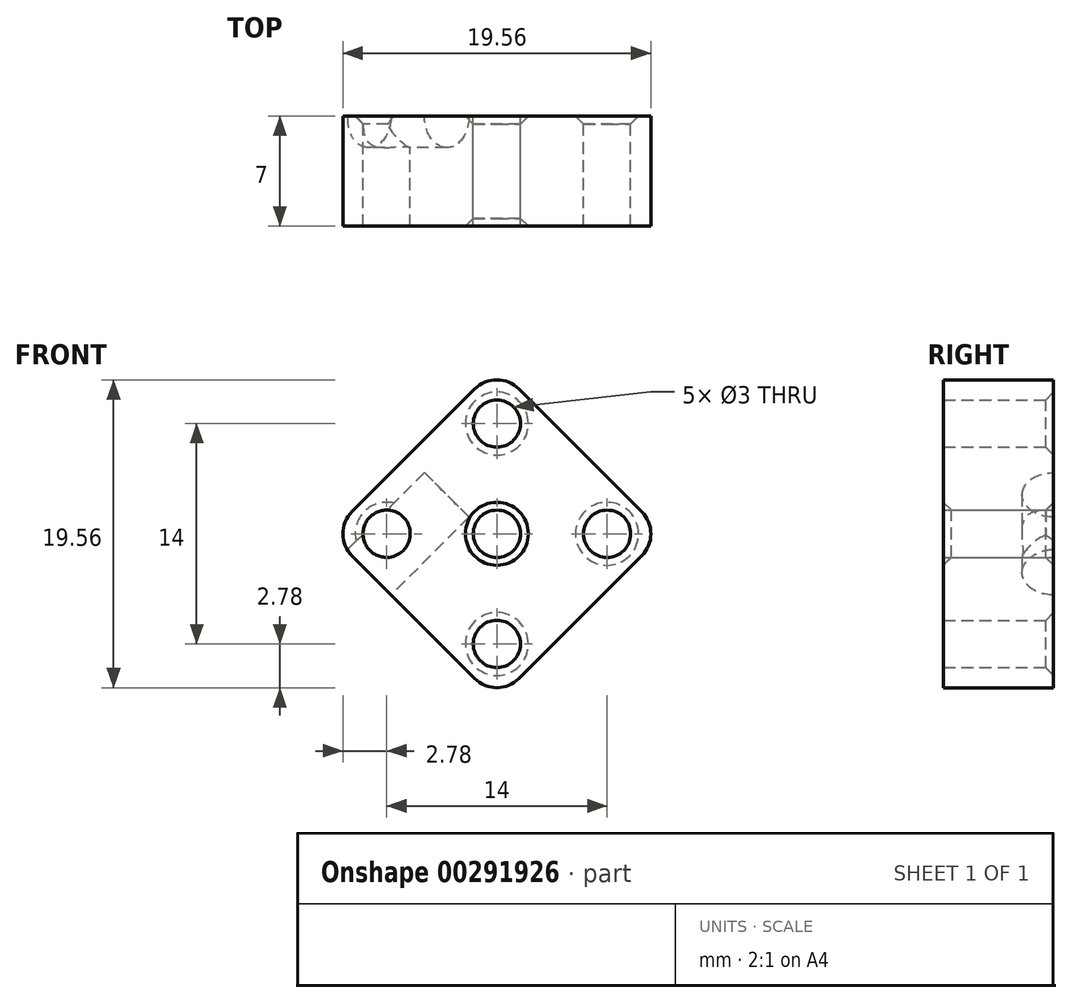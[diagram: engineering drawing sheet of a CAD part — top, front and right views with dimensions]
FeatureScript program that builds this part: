
annotation { "Feature Type Name" : "Feature", "Feature Type Description" : "" }
export const myFeature = defineFeature(function(context is Context, id is Id, definition is map)
    precondition{}
    {
        {
            var Q0;
            Q0=qCreatedBy(makeId("Front.planeOp"),FACE);
            var sketch = newSketch(context, id + "F0", { "sketchPlane" : qUnion([Q0])});
            skLineSegment(sketch, "E0.bottom", {"start": v(-1.41, -9.2) * mm, "end": v(-9.2, -1.41) * mm});
            skLineSegment(sketch, "E0.top", {"start": v(9.2, 1.41) * mm, "end": v(1.41, 9.2) * mm});
            skLineSegment(sketch, "E0.left", {"start": v(1.41, -9.2) * mm, "end": v(9.2, -1.41) * mm});
            skLineSegment(sketch, "E0.right", {"start": v(-9.2, 1.41) * mm, "end": v(-1.41, 9.2) * mm});
            skCircle(sketch, "E1", {"center": v(0, 7) * mm, "radius": 1.5 * mm});
            skCircle(sketch, "E2", {"center": v(0, 0) * mm, "radius": 1.5 * mm});
            skCircle(sketch, "E3.1.1", {"center": v(-7, 0) * mm, "radius": 1.5 * mm});
            skCircle(sketch, "E3.2.1", {"center": v(0, -7) * mm, "radius": 1.5 * mm});
            skCircle(sketch, "E3.3.1", {"center": v(7, 0) * mm, "radius": 1.5 * mm});
            skPoint(sketch, "E4.visualSharp", {"position": v(-10.6, 0) * mm});
            skArc(sketch, "E4.filletArc", {"start": v(-9.2, 1.41) * mm, "mid": v(-9.78, 0) * mm, "end": v(-9.2, -1.41) * mm});
            skPoint(sketch, "E5.visualSharp", {"position": v(0, -10.6) * mm});
            skArc(sketch, "E5.filletArc", {"start": v(-1.41, -9.2) * mm, "mid": v(0, -9.78) * mm, "end": v(1.41, -9.2) * mm});
            skPoint(sketch, "E6.visualSharp", {"position": v(10.6, 0) * mm});
            skArc(sketch, "E6.filletArc", {"start": v(9.2, -1.41) * mm, "mid": v(9.78, 0) * mm, "end": v(9.2, 1.41) * mm});
            skPoint(sketch, "E7.visualSharp", {"position": v(0, 10.6) * mm});
            skArc(sketch, "E7.filletArc", {"start": v(1.41, 9.2) * mm, "mid": v(0, 9.78) * mm, "end": v(-1.41, 9.2) * mm});
            skSolve(sketch);
        }
        {
            var Q0;
            Q0=makeQuery(id+"F0.imprint","IMPRINT",FACE,{"disambiguationData":[TD([[makeQuery(id+"F0.imprint","IMPRINT",EDGE,{"derivedFrom":sQuery(id+"F0.wireOp",EDGE,"E0.bottom")}),-1.0]])]});
            extrude(context, id + "F1", {"entities" : qUnion([Q0]), "depth" : 7 * mm});
        }
        {
            var Q0;
            Q0=makeQuery(id+"F1.opExtrude","SWEPT_FACE",FACE,{"disambiguationData":[OSD([sQuery(id+"F0.wireOp",EDGE,"E0.bottom")])]});
            var sketch = newSketch(context, id + "F2", { "sketchPlane" : qUnion([Q0])});
            skCircle(sketch, "E8", {"center": v(0, 4) * mm, "radius": 2 * mm});
            skSolve(sketch);
        }
        {
            var Q0;
            Q0=makeQuery(id+"F2.imprint","IMPRINT",FACE,{"disambiguationData":[TD([[makeQuery(id+"F2.imprint","IMPRINT",EDGE,{"derivedFrom":sQuery(id+"F2.wireOp",EDGE,"E8")}),1.0]])]});
            extrude(context, id + "F3", {"entities" : qUnion([Q0]), "operationType" : NewBodyOperationType.REMOVE, "oppositeDirection" : true, "offsetDistance" : 25 * mm, "depth" : 7 * mm});
        }
        {
            var Q0;
            Q0=makeQuery(id+"F1.opExtrude","CAP_EDGE",EDGE,{"disambiguationData":[OSD([sQuery(id+"F0.wireOp",EDGE,"E1")])],"isStart":true});
            var Q1;
            Q1=makeQuery(id+"F1.opExtrude","CAP_EDGE",EDGE,{"disambiguationData":[OSD([sQuery(id+"F0.wireOp",EDGE,"E3.1.1")])],"isStart":true});
            var Q2;
            Q2=makeQuery(id+"F1.opExtrude","CAP_EDGE",EDGE,{"disambiguationData":[OSD([sQuery(id+"F0.wireOp",EDGE,"E3.2.1")])],"isStart":true});
            var Q3;
            Q3=makeQuery(id+"F1.opExtrude","CAP_EDGE",EDGE,{"disambiguationData":[OSD([sQuery(id+"F0.wireOp",EDGE,"E3.3.1")])],"isStart":true});
            var Q4;
            Q4=makeQuery(id+"F1.opExtrude","CAP_EDGE",EDGE,{"disambiguationData":[OSD([sQuery(id+"F0.wireOp",EDGE,"E2")])],"isStart":false});
            var Q5;
            Q5=makeQuery(id+"F3.boolean.opBoolean","COPY",EDGE,{"derivedFrom":makeQuery(id+"F3.opExtrude","CAP_EDGE",EDGE,{"disambiguationData":[OSD([sQuery(id+"F2.wireOp",EDGE,"E8")])],"isStart":true})});
            chamfer(context, id + "F4", {"entities" : qUnion([Q0, Q1, Q2, Q3, Q4, Q5]), "width" : 0.5 * mm, "tangentPropagation" : true});
        }
    });
